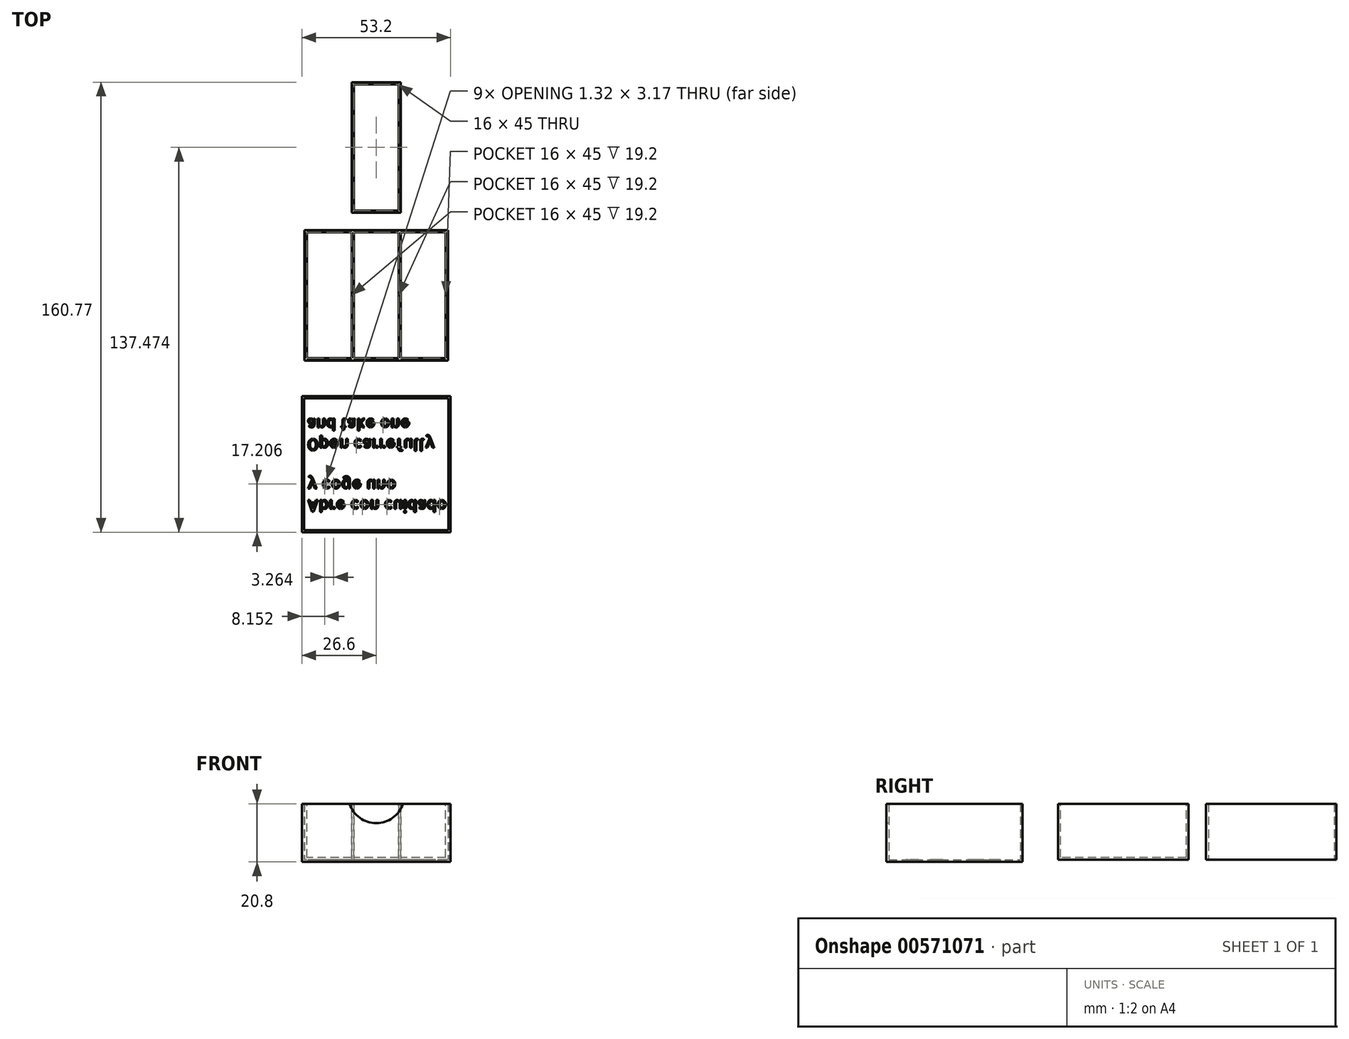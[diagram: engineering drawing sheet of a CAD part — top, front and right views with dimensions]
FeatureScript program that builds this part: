
annotation { "Feature Type Name" : "Feature", "Feature Type Description" : "" }
export const myFeature = defineFeature(function(context is Context, id is Id, definition is map)
    precondition{}
    {
        {
            var Q0;
            Q0=qCreatedBy(makeId("Top.planeOp"),FACE);
            var sketch = newSketch(context, id + "F0", { "sketchPlane" : qUnion([Q0])});
            skLineSegment(sketch, "E0.bottom", {"start": v(25.6, 23.3) * mm, "end": v(-25.6, 23.3) * mm});
            skLineSegment(sketch, "E0.top", {"start": v(25.6, -23.3) * mm, "end": v(-25.6, -23.3) * mm});
            skLineSegment(sketch, "E0.left", {"start": v(25.6, 23.3) * mm, "end": v(25.6, -23.3) * mm});
            skLineSegment(sketch, "E0.right", {"start": v(-25.6, 23.3) * mm, "end": v(-25.6, -23.3) * mm});
            skPoint(sketch, "E0.middle", {"position": v(0, 0) * mm});
            skSolve(sketch);
        }
        {
            var Q0;
            Q0=makeQuery(id+"F0.imprint","IMPRINT",FACE,{"disambiguationData":[TD([[makeQuery(id+"F0.imprint","IMPRINT",EDGE,{"derivedFrom":sQuery(id+"F0.wireOp",EDGE,"E0.bottom")}),1.0]])]});
            extrude(context, id + "F1", {"entities" : qUnion([Q0]), "depth" : 20 * mm, "offsetDistance" : 25 * mm});
        }
        {
            var Q0;
            Q0=makeQuery(id+"F1.opExtrude","CAP_FACE",FACE,{"disambiguationData":[OSD([sQuery(id+"F0.wireOp",EDGE,"E0.bottom"),sQuery(id+"F0.wireOp",EDGE,"E0.top"),sQuery(id+"F0.wireOp",EDGE,"E0.left"),sQuery(id+"F0.wireOp",EDGE,"E0.right")])],"isStart":false});
            var sketch = newSketch(context, id + "F2", { "sketchPlane" : qUnion([Q0])});
            skLineSegment(sketch, "E1.bottom", {"start": v(8, 22.5) * mm, "end": v(-8, 22.5) * mm});
            skLineSegment(sketch, "E1.top", {"start": v(8, -22.5) * mm, "end": v(-8, -22.5) * mm});
            skLineSegment(sketch, "E1.left", {"start": v(8, 22.5) * mm, "end": v(8, -22.5) * mm});
            skLineSegment(sketch, "E1.right", {"start": v(-8, 22.5) * mm, "end": v(-8, -22.5) * mm});
            skPoint(sketch, "E1.middle", {"position": v(0, 0) * mm});
            skLineSegment(sketch, "E2.1.0.0", {"start": v(24.8, 22.5) * mm, "end": v(24.8, -22.5) * mm});
            skLineSegment(sketch, "E2.1.0.1", {"start": v(24.8, 22.5) * mm, "end": v(8.8, 22.5) * mm});
            skLineSegment(sketch, "E2.1.0.2", {"start": v(8.8, 22.5) * mm, "end": v(8.8, -22.5) * mm});
            skLineSegment(sketch, "E2.1.0.3", {"start": v(24.8, -22.5) * mm, "end": v(8.8, -22.5) * mm});
            skLineSegment(sketch, "E2.direction1", {"start": v(8, -22.5) * mm, "end": v(24.8, -22.5) * mm, "construction": true});
            skLineSegment(sketch, "E3.1.0.0", {"start": v(-8.8, 22.5) * mm, "end": v(-24.8, 22.5) * mm});
            skLineSegment(sketch, "E3.1.0.1", {"start": v(-24.8, 22.5) * mm, "end": v(-24.8, -22.5) * mm});
            skLineSegment(sketch, "E3.1.0.2", {"start": v(-8.8, 22.5) * mm, "end": v(-8.8, -22.5) * mm});
            skLineSegment(sketch, "E3.1.0.3", {"start": v(-8.8, -22.5) * mm, "end": v(-24.8, -22.5) * mm});
            skLineSegment(sketch, "E3.direction1", {"start": v(-8, 22.5) * mm, "end": v(-24.8, 22.5) * mm, "construction": true});
            skSolve(sketch);
        }
        {
            var Q0;
            Q0=makeQuery(id+"F2.imprint","IMPRINT",FACE,{"disambiguationData":[TD([[makeQuery(id+"F2.imprint","IMPRINT",EDGE,{"derivedFrom":sQuery(id+"F2.wireOp",EDGE,"E3.1.0.0")}),1.0]])]});
            var Q1;
            Q1=makeQuery(id+"F2.imprint","IMPRINT",FACE,{"disambiguationData":[TD([[makeQuery(id+"F2.imprint","IMPRINT",EDGE,{"derivedFrom":sQuery(id+"F2.wireOp",EDGE,"E1.bottom")}),1.0]])]});
            var Q2;
            Q2=makeQuery(id+"F2.imprint","IMPRINT",FACE,{"disambiguationData":[TD([[makeQuery(id+"F2.imprint","IMPRINT",EDGE,{"derivedFrom":sQuery(id+"F2.wireOp",EDGE,"E2.1.0.0")}),-1.0]])]});
            extrude(context, id + "F3", {"entities" : qUnion([Q0, Q1, Q2]), "operationType" : NewBodyOperationType.REMOVE, "oppositeDirection" : true, "depth" : 19.2 * mm, "offsetDistance" : 25 * mm});
        }
        {
            var Q0;
            Q0=qCreatedBy(makeId("Top.planeOp"),FACE);
            var sketch = newSketch(context, id + "F4", { "sketchPlane" : qUnion([Q0])});
            skLineSegment(sketch, "E4.bottom", {"start": v(25.8, -83.85) * mm, "end": v(-25.8, -83.85) * mm});
            skLineSegment(sketch, "E4.top", {"start": v(25.8, -36.85) * mm, "end": v(-25.8, -36.85) * mm});
            skLineSegment(sketch, "E4.left", {"start": v(25.8, -83.85) * mm, "end": v(25.8, -36.85) * mm});
            skLineSegment(sketch, "E4.right", {"start": v(-25.8, -83.85) * mm, "end": v(-25.8, -36.85) * mm});
            skPoint(sketch, "E4.middle", {"position": v(0, -60.35) * mm});
            skSolve(sketch);
        }
        {
            var Q0;
            Q0=makeQuery(id+"F4.imprint","IMPRINT",FACE,{"disambiguationData":[TD([[makeQuery(id+"F4.imprint","IMPRINT",EDGE,{"derivedFrom":sQuery(id+"F4.wireOp",EDGE,"E4.bottom")}),-1.0]])]});
            extrude(context, id + "F5", {"entities" : qUnion([Q0]), "depth" : 20 * mm, "offsetDistance" : 25 * mm});
        }
        {
            var Q0;
            Q0=makeQuery(id+"F5.opExtrude","CAP_FACE",FACE,{"disambiguationData":[OSD([sQuery(id+"F4.wireOp",EDGE,"E4.bottom"),sQuery(id+"F4.wireOp",EDGE,"E4.top"),sQuery(id+"F4.wireOp",EDGE,"E4.left"),sQuery(id+"F4.wireOp",EDGE,"E4.right")])],"isStart":false});
            shell(context, id + "F6", {"entities" : qUnion([Q0]), "thickness" : .8 * mm, "oppositeDirection" : true});
        }
        {
            var Q0;
            Q0=makeQuery(id+"F5.opExtrude","SWEPT_FACE",FACE,{"disambiguationData":[OSD([sQuery(id+"F4.wireOp",EDGE,"E4.bottom")])]});
            var sketch = newSketch(context, id + "F7", { "sketchPlane" : qUnion([Q0])});
            skLineSegment(sketch, "E5.0.0", {"start": v(-26.6, -0.8) * mm, "end": v(26.6, -0.8) * mm, "construction": true});
            skLineSegment(sketch, "E5.0.1", {"start": v(26.6, -0.8) * mm, "end": v(26.6, 20) * mm, "construction": true});
            skLineSegment(sketch, "E5.0.2", {"start": v(26.6, 20) * mm, "end": v(-26.6, 20) * mm, "construction": true});
            skLineSegment(sketch, "E5.0.3", {"start": v(-26.6, 20) * mm, "end": v(-26.6, -0.8) * mm, "construction": true});
            skLineSegment(sketch, "E6", {"start": v(0, 20) * mm, "end": v(0, 0) * mm, "construction": true});
            skArc(sketch, "E7", {"start": v(-9.5, 20) * mm, "mid": v(0, 13.04) * mm, "end": v(9.5, 20) * mm});
            skSolve(sketch);
        }
        {
            var Q0;
            {var subQ0=sQuery(id+"F7.wireOp",EDGE,"E7");Q0=makeQuery(id+"F7.imprint","IMPRINT",FACE,{"disambiguationData":[TD([[makeQuery(id+"F7.imprint","IMPRINT",EDGE,{"derivedFrom":subQ0}),1.0]])]});}
            var Q1;
            Q1=makeQuery(id+"F5.opExtrude","SWEPT_FACE",FACE,{"disambiguationData":[OSD([sQuery(id+"F4.wireOp",EDGE,"E4.top")])]});
            extrude(context, id + "F8", {"entities" : qUnion([Q0]), "operationType" : NewBodyOperationType.REMOVE, "endBound" : BoundingType.UP_TO_SURFACE, "oppositeDirection" : true, "depth" : 25 * mm, "endBoundEntityFace" : qUnion([Q1]), "offsetDistance" : 25 * mm});
        }
        {
            var Q0;
            Q0=qCreatedBy(makeId("Top.planeOp"),FACE);
            var sketch = newSketch(context, id + "F9", { "sketchPlane" : qUnion([Q0])});
            skLineSegment(sketch, "E8.bottom", {"start": v(8, 75.32) * mm, "end": v(-8, 75.32) * mm});
            skLineSegment(sketch, "E8.top", {"start": v(8, 30.32) * mm, "end": v(-8, 30.32) * mm});
            skLineSegment(sketch, "E8.left", {"start": v(8, 75.32) * mm, "end": v(8, 30.32) * mm});
            skLineSegment(sketch, "E8.right", {"start": v(-8, 75.32) * mm, "end": v(-8, 30.32) * mm});
            skPoint(sketch, "E8.middle", {"position": v(0, 52.82) * mm});
            skSolve(sketch);
        }
        {
            var Q0;
            Q0=makeQuery(id+"F9.imprint","IMPRINT",FACE,{"disambiguationData":[TD([[makeQuery(id+"F9.imprint","IMPRINT",EDGE,{"derivedFrom":sQuery(id+"F9.wireOp",EDGE,"E8.bottom")}),1.0]])]});
            extrude(context, id + "F10", {"entities" : qUnion([Q0]), "depth" : 20 * mm, "offsetDistance" : 25 * mm});
        }
        {
            var Q0;
            Q0=makeQuery(id+"F10.opExtrude","CAP_FACE",FACE,{"disambiguationData":[OSD([sQuery(id+"F9.wireOp",EDGE,"E8.bottom"),sQuery(id+"F9.wireOp",EDGE,"E8.top"),sQuery(id+"F9.wireOp",EDGE,"E8.left"),sQuery(id+"F9.wireOp",EDGE,"E8.right")])],"isStart":false});
            var Q1;
            Q1=makeQuery(id+"F10.opExtrude","CAP_FACE",FACE,{"disambiguationData":[OSD([sQuery(id+"F9.wireOp",EDGE,"E8.bottom"),sQuery(id+"F9.wireOp",EDGE,"E8.top"),sQuery(id+"F9.wireOp",EDGE,"E8.left"),sQuery(id+"F9.wireOp",EDGE,"E8.right")])],"isStart":true});
            shell(context, id + "F11", {"entities" : qUnion([Q0, Q1]), "thickness" : .8 * mm, "oppositeDirection" : true});
        }
        {
            var Q0;
            Q0=makeQuery(id+"F5.opExtrude","CAP_FACE",FACE,{"disambiguationData":[OSD([sQuery(id+"F4.wireOp",EDGE,"E4.bottom"),sQuery(id+"F4.wireOp",EDGE,"E4.top"),sQuery(id+"F4.wireOp",EDGE,"E4.left"),sQuery(id+"F4.wireOp",EDGE,"E4.right")])],"isStart":true});
            var sketch = newSketch(context, id + "F12", { "sketchPlane" : qUnion([Q0])});
            skText(sketch, "E9", { "text": "Abre con cuidado\ny coge uno\n\nOpen carrefully\nand take one", "fontName": "AllertaStencil-Regular.ttf"});
            const initialGuessF12  = {"E9": [-0.02476, 0.07317, 1, 0, 0.0041]};
            skSetInitialGuess(sketch, initialGuessF12);
            skSolve(sketch);
        }
        {
            var Q0;
            Q0 = qSketchRegion(id + "F12", true);
            extrude(context, id + "F13", {"entities" : qUnion([Q0]), "operationType" : NewBodyOperationType.REMOVE, "endBound" : BoundingType.THROUGH_ALL, "oppositeDirection" : true, "depth" : 25 * mm, "offsetDistance" : 25 * mm});
        }
    });
